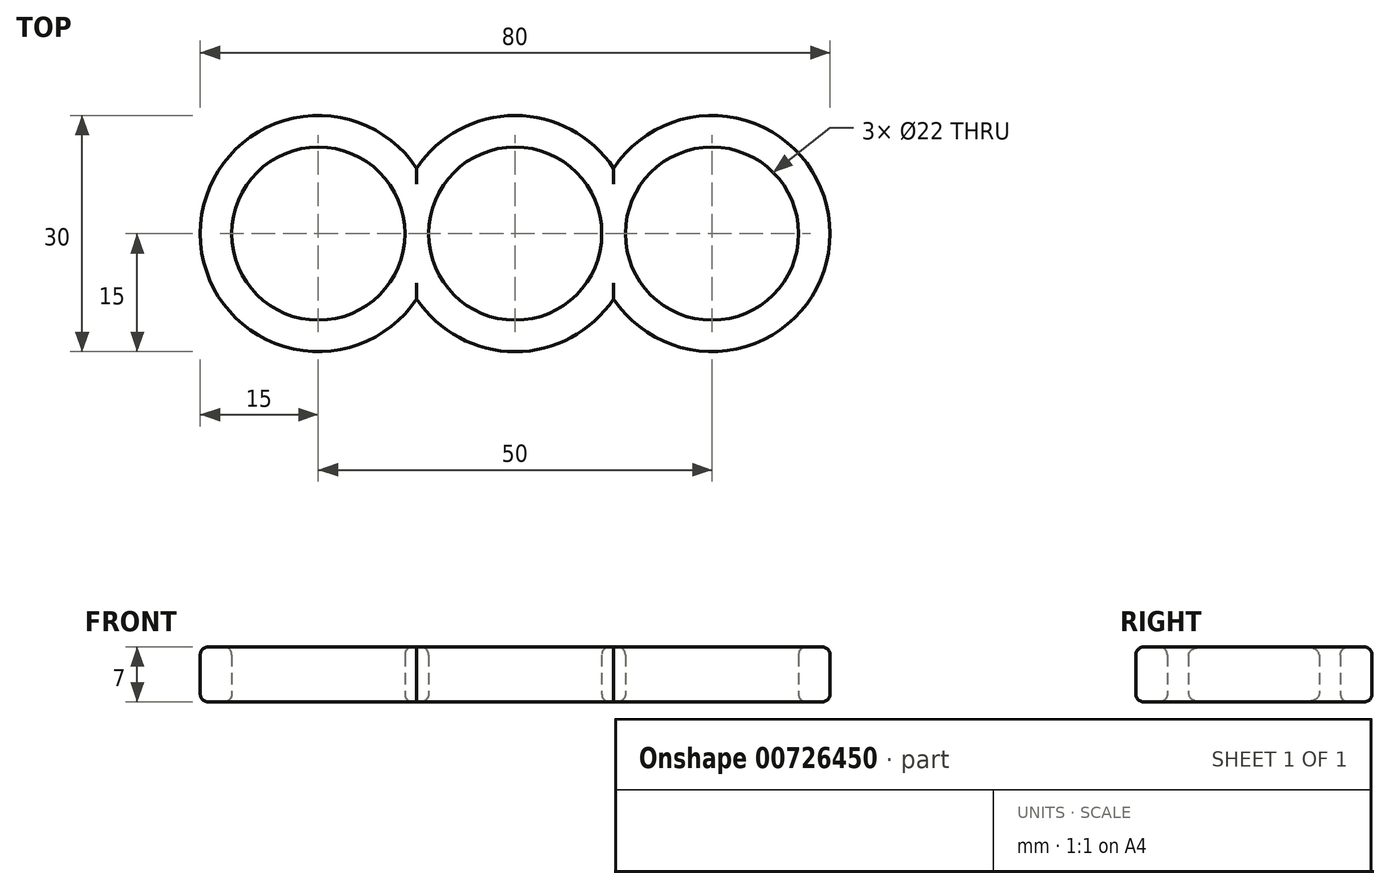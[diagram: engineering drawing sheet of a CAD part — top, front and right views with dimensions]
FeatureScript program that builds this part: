
annotation { "Feature Type Name" : "Feature", "Feature Type Description" : "" }
export const myFeature = defineFeature(function(context is Context, id is Id, definition is map)
    precondition{}
    {
        {
            var Q0;
            Q0=qCreatedBy(makeId("Top.planeOp"),FACE);
            var sketch = newSketch(context, id + "F0", { "sketchPlane" : qUnion([Q0])});
            skArc(sketch, "E0", {"start": v(0, 11) * mm, "mid": v(-11, 0) * mm, "end": v(0, -11) * mm});
            skArc(sketch, "E1", {"start": v(-12.5, -8.3) * mm, "mid": v(-7.1, -13.22) * mm, "end": v(0, -15) * mm});
            skLineSegment(sketch, "E2", {"start": v(-10, 0) * mm, "end": v(-11, 0) * mm});
            skCircle(sketch, "E3", {"center": v(-25, 0) * mm, "radius": 11 * mm});
            skArc(sketch, "E4", {"start": v(-12.5, 8.3) * mm, "mid": v(-40, 0) * mm, "end": v(-12.5, -8.3) * mm});
            skLineSegment(sketch, "E5.trimOffspring", {"start": v(-14, 0) * mm, "end": v(-15, 0) * mm});
            skArc(sketch, "E6.trimOffspring", {"start": v(0, 15) * mm, "mid": v(-7.1, 13.22) * mm, "end": v(-12.5, 8.3) * mm});
            skLineSegment(sketch, "E7.MirrorCS", {"start": v(10, 0) * mm, "end": v(11, 0) * mm});
            skLineSegment(sketch, "E8.MirrorCS", {"start": v(14, 0) * mm, "end": v(15, 0) * mm});
            skArc(sketch, "E9.MirrorCS", {"start": v(12.5, -8.3) * mm, "mid": v(7.1, -13.22) * mm, "end": v(0, -15) * mm});
            skArc(sketch, "E10.MirrorCS", {"start": v(0, 11) * mm, "mid": v(11, 0) * mm, "end": v(0, -11) * mm});
            skCircle(sketch, "E11.MirrorC", {"center": v(25, 0) * mm, "radius": 11 * mm});
            skArc(sketch, "E12.MirrorCS", {"start": v(0, 15) * mm, "mid": v(7.1, 13.22) * mm, "end": v(12.5, 8.3) * mm});
            skArc(sketch, "E13.MirrorCS", {"start": v(12.5, 8.3) * mm, "mid": v(40, 0) * mm, "end": v(12.5, -8.3) * mm});
            skSolve(sketch);
        }
        {
            var Q0;
            Q0 = qSketchRegion(id + "F0", true);
            extrude(context, id + "F1", {"entities" : qUnion([Q0]), "depth" : 7 * mm, "offsetDistance" : 25 * mm});
        }
        {
            var Q0;
            Q0=makeQuery(id+"F1.opExtrude","CAP_FACE",FACE,{"disambiguationData":[OSD([sQuery(id+"F0.wireOp",EDGE,"E0"),sQuery(id+"F0.wireOp",EDGE,"E1"),sQuery(id+"F0.wireOp",EDGE,"E3"),sQuery(id+"F0.wireOp",EDGE,"E4"),sQuery(id+"F0.wireOp",EDGE,"E6.trimOffspring"),sQuery(id+"F0.wireOp",EDGE,"E9.MirrorCS"),sQuery(id+"F0.wireOp",EDGE,"E10.MirrorCS"),sQuery(id+"F0.wireOp",EDGE,"E11.MirrorC"),sQuery(id+"F0.wireOp",EDGE,"E12.MirrorCS"),sQuery(id+"F0.wireOp",EDGE,"E13.MirrorCS")])],"isStart":false});
            fillet(context, id + "F2", {"entities" : qUnion([Q0]), "radius" : 1 * mm, "tangentPropagation" : true, "allowEdgeOverflow" : false});
        }
        {
            var Q0;
            Q0=makeQuery(id+"F1.opExtrude","CAP_FACE",FACE,{"disambiguationData":[OSD([sQuery(id+"F0.wireOp",EDGE,"E0"),sQuery(id+"F0.wireOp",EDGE,"E1"),sQuery(id+"F0.wireOp",EDGE,"E3"),sQuery(id+"F0.wireOp",EDGE,"E4"),sQuery(id+"F0.wireOp",EDGE,"E6.trimOffspring"),sQuery(id+"F0.wireOp",EDGE,"E9.MirrorCS"),sQuery(id+"F0.wireOp",EDGE,"E10.MirrorCS"),sQuery(id+"F0.wireOp",EDGE,"E11.MirrorC"),sQuery(id+"F0.wireOp",EDGE,"E12.MirrorCS"),sQuery(id+"F0.wireOp",EDGE,"E13.MirrorCS")])],"isStart":true});
            fillet(context, id + "F3", {"entities" : qUnion([Q0]), "radius" : 1 * mm, "tangentPropagation" : true, "allowEdgeOverflow" : false});
        }
    });
